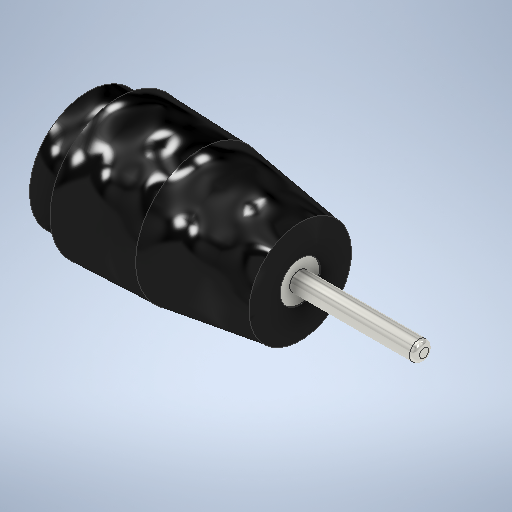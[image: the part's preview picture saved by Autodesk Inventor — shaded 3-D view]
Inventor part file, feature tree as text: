
AUTODESK INVENTOR PART (.ipt)
format: ipt  version: 2025 (Build 290162000, 162)  size: 300,032 bytes
history: native  units: in
note: dims shown in document units (in); Inventor stores cm internally (conversion verified against a paired STEP export)
features: sketch x3, extrude x2, revolve x1
ambient origin geometry x8: Origin, YZ Plane, XZ Plane, XY Plane, X Axis, Y Axis, Z Axis, Center Point
bodies: Solid1 (feature_tree)
feature tree (6):
  revolve  "Revolution1"  [1 undecoded]
  extrude  "Extrusion1"  Depth=0.7087in
  extrude  "Extrusion2"  Depth=0.0197in
  sketch  "Sketch1"  dims[d0=0.2264in d1=0.1181in]
  sketch  "Sketch2"  dims[d2=0.0394in d3=0.7087in]
  sketch  "Sketch3"  dims[d5=0.4803in d6=0.0197in d7=90.0deg d8=0.1575in d9=0.7874in d10=0.0in d11=0.0374in d12=0.1575in d13=0.0039in d14=0.0in]
note: 1 required parameter value undecoded (feature->parameter linkage not recoverable at this tier; creation-order binding heuristic only, values carry confidence <= 0.55)
